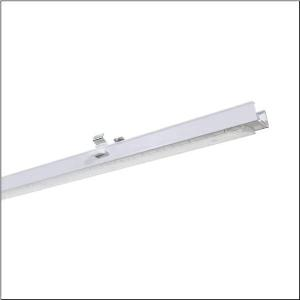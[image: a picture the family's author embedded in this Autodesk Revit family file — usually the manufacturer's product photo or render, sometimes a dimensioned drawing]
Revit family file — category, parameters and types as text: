
# Revit family: trunking_flex_31_51re12mb68b
name_source: partatom
category: Lighting Fixtures
units: mm (PartAtom-declared; Revit-internal decimal feet)

## family parameters
Cut with Voids When Loaded = No
Host = Face
Light Source = No
Part Type = Normal
Room Calculation Point = No
Round Connector Dimension = Use Diameter
Shared = No

## types (1)
- --- (1 x LED, 8000 lm, 50 W, 6500K)
    Apparent Load = 50 VA
    CIE Flux Codes = 65 91 98 99 100
    Color Rendering = 80
    Color Temperature = 6500K
    Default Elevation = 1800 mm
    Description = Trunking Flex 31, luminaire insert, of extruded aluminium section, coated, traffic white (RAL 9016), length: 1.472mm, width: 91mm, height: 53mm, LED rated luminous flux: 8.000lm, light colour: 865, control gear: ON/OFF Multilumen, with system connector: socket, mains connection: 220..240V, AC, 50/60Hz, rated input power: 50W, luminous flux adjustable on luminaire in four steps (4130/5610/6850/8000lm), connected load according to luminous flux setting (25/34/42/50W), primary light control with lens, of plastic, primary optical cover: cover, of PMMA, light emission: direct distribution, protection rating (complete): IP20, insulation class (complete): insulation class I (protective earthing), certification: CE, UKCA, impact resistance: IK02, permissible ambient temperature for indoor applications: -20..+40°C, packaging unit: 1 piece
    Height = 58 mm
    Lamp = 1 x LED
    Lamp Light Flux = 8000 lm
    Lamp Power = 50 W
    Lamp count = 1
    Length = 1472 mm
    Luminous efficacy = 160 lm/W
    Manufacturer = Siteco
    ModVariant = No
    Model = 51RE12MB68B
    Mounting Place = Ceiling
    Mounting Type = Pendant
    Number of Poles = 1
    OnlyDefault = Yes
    Power Factor = 1
    Product Name = Trunking Flex 31
    Product group = luminaire insert
    ProductGroupID = 901
    Protection Class = Protection class I
    Protection Degree = IP 20
    RLX_Detail_Level = 1
    RLX_Emergency_Light_Flux = 0 lm
    RLX_Emergency_Type = 0
    RLX_Emergency_Type_DB = No
    RlxData = <blob elided: 20289 chars, md5=52b74afc>
    Socket = socket
    Standby Power = 0 W
    System Light Flux = 8000 lm
    System Power = 50 W
    Type Comments = factory setting: luminous flux: 100 % | (ON | ON) | 300 mA
    Type Image = l_1266702.jpg
    URL = http://relux.com
    VarID = @adj_001225
    Voltage = 0 V
    Weight = 0.00 kg
    Width = 65 mm

## geometry (parser evidence)
native form markers: Blend x4, Sweep x10
no freeform markers — native parametric forms only
